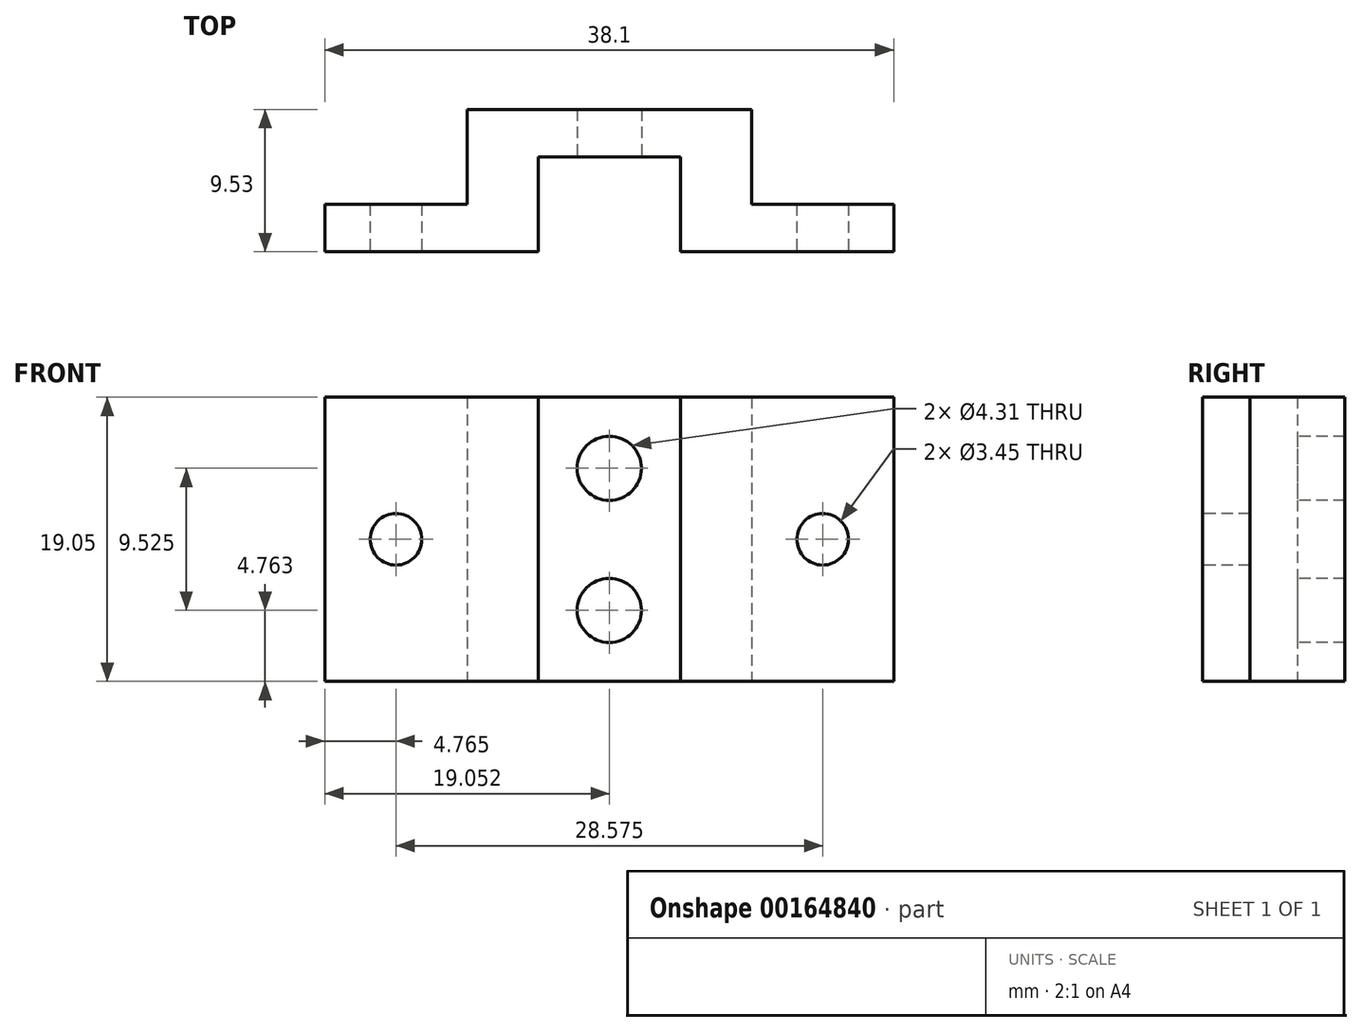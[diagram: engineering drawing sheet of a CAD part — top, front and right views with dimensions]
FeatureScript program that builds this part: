
annotation { "Feature Type Name" : "Feature", "Feature Type Description" : "" }
export const myFeature = defineFeature(function(context is Context, id is Id, definition is map)
    precondition{}
    {
        {
            var Q0;
            Q0=qCreatedBy(makeId("Top.planeOp"),FACE);
            var sketch = newSketch(context, id + "F0", { "sketchPlane" : qUnion([Q0])});
            skLineSegment(sketch, "E0.bottom", {"start": v(0, 0) * mm, "end": v(9.53, 0) * mm, "construction": true});
            skLineSegment(sketch, "E0.top", {"start": v(0, 6.35) * mm, "end": v(9.53, 6.35) * mm});
            skLineSegment(sketch, "E0.left", {"start": v(0, 0) * mm, "end": v(0, 6.35) * mm});
            skLineSegment(sketch, "E0.right", {"start": v(9.53, 0) * mm, "end": v(9.53, 6.35) * mm});
            skLineSegment(sketch, "E1", {"start": v(4.76, 6.35) * mm, "end": v(4.76, 9.53) * mm, "construction": true});
            skLineSegment(sketch, "E2", {"start": v(-4.76, 9.53) * mm, "end": v(14.29, 9.53) * mm});
            skLineSegment(sketch, "E3", {"start": v(9.53, 6.35) * mm, "end": v(14.29, 6.35) * mm, "construction": true});
            skLineSegment(sketch, "E4", {"start": v(14.29, 9.53) * mm, "end": v(14.29, 3.17) * mm});
            skLineSegment(sketch, "E5", {"start": v(9.53, 0) * mm, "end": v(23.81, 0) * mm});
            skLineSegment(sketch, "E6", {"start": v(23.81, 0) * mm, "end": v(23.81, 3.17) * mm});
            skLineSegment(sketch, "E7", {"start": v(14.29, 3.17) * mm, "end": v(23.81, 3.18) * mm});
            skLineSegment(sketch, "E8", {"start": v(-4.76, 9.53) * mm, "end": v(-4.76, 3.17) * mm});
            skLineSegment(sketch, "E9", {"start": v(-4.76, 3.17) * mm, "end": v(-14.29, 3.17) * mm});
            skLineSegment(sketch, "E10", {"start": v(-14.29, 3.17) * mm, "end": v(-14.29, 0) * mm});
            skLineSegment(sketch, "E11", {"start": v(-14.29, 0) * mm, "end": v(0, 0) * mm});
            skSolve(sketch);
        }
        {
            var Q0;
            Q0 = qSketchRegion(id + "F0", true);
            extrude(context, id + "F1", {"entities" : qUnion([Q0]), "depth" : 19.05 * mm});
        }
        {
            var Q0;
            Q0=makeQuery(id+"F1.opExtrude","SWEPT_FACE",FACE,{"disambiguationData":[OSD([sQuery(id+"F0.wireOp",EDGE,"E11")])]});
            var sketch = newSketch(context, id + "F2", { "sketchPlane" : qUnion([Q0])});
            skLineSegment(sketch, "E12.bottom", {"start": v(4.76, 0) * mm, "end": v(0, 0) * mm, "construction": true});
            skLineSegment(sketch, "E12.top", {"start": v(4.76, 4.76) * mm, "end": v(0, 4.76) * mm, "construction": true});
            skLineSegment(sketch, "E12.left", {"start": v(4.76, 0) * mm, "end": v(4.76, 4.76) * mm, "construction": true});
            skLineSegment(sketch, "E12.right", {"start": v(0, 0) * mm, "end": v(0, 4.76) * mm, "construction": true});
            skLineSegment(sketch, "E13.bottom", {"start": v(4.76, 19.05) * mm, "end": v(9.53, 19.05) * mm, "construction": true});
            skLineSegment(sketch, "E13.top", {"start": v(4.76, 14.29) * mm, "end": v(9.53, 14.29) * mm, "construction": true});
            skLineSegment(sketch, "E13.left", {"start": v(4.76, 19.05) * mm, "end": v(4.76, 14.29) * mm, "construction": true});
            skLineSegment(sketch, "E13.right", {"start": v(9.53, 19.05) * mm, "end": v(9.53, 14.29) * mm, "construction": true});
            skCircle(sketch, "E14", {"center": v(4.76, 4.76) * mm, "radius": 2.15 * mm});
            skCircle(sketch, "E15", {"center": v(4.76, 14.29) * mm, "radius": 2.15 * mm});
            skLineSegment(sketch, "E16.bottom", {"start": v(-9.53, 9.53) * mm, "end": v(-14.29, 9.53) * mm, "construction": true});
            skLineSegment(sketch, "E16.top", {"start": v(-9.53, 19.05) * mm, "end": v(-14.29, 19.05) * mm, "construction": true});
            skLineSegment(sketch, "E16.left", {"start": v(-14.29, 9.53) * mm, "end": v(-14.29, 19.05) * mm, "construction": true});
            skLineSegment(sketch, "E16.right", {"start": v(-9.53, 9.53) * mm, "end": v(-9.53, 19.05) * mm, "construction": true});
            skLineSegment(sketch, "E17.bottom", {"start": v(19.05, 9.53) * mm, "end": v(23.81, 9.53) * mm, "construction": true});
            skLineSegment(sketch, "E17.top", {"start": v(19.05, 19.05) * mm, "end": v(23.81, 19.05) * mm, "construction": true});
            skLineSegment(sketch, "E17.left", {"start": v(23.81, 9.53) * mm, "end": v(23.81, 19.05) * mm, "construction": true});
            skLineSegment(sketch, "E17.right", {"start": v(19.05, 9.53) * mm, "end": v(19.05, 19.05) * mm, "construction": true});
            skCircle(sketch, "E18", {"center": v(-9.53, 9.53) * mm, "radius": 1.73 * mm});
            skCircle(sketch, "E19", {"center": v(19.05, 9.53) * mm, "radius": 1.73 * mm});
            skSolve(sketch);
        }
        {
            var Q0;
            Q0 = qSketchRegion(id + "F2", true);
            var Q1;
            Q1=makeQuery(id+"F1.opExtrude","SWEPT_FACE",FACE,{"disambiguationData":[OSD([sQuery(id+"F0.wireOp",EDGE,"E2")])]});
            extrude(context, id + "F3", {"entities" : qUnion([Q0]), "operationType" : NewBodyOperationType.REMOVE, "endBound" : BoundingType.UP_TO_SURFACE, "oppositeDirection" : true, "endBoundEntityFace" : qUnion([Q1]), "depth" : 25.4 * mm});
        }
    });
